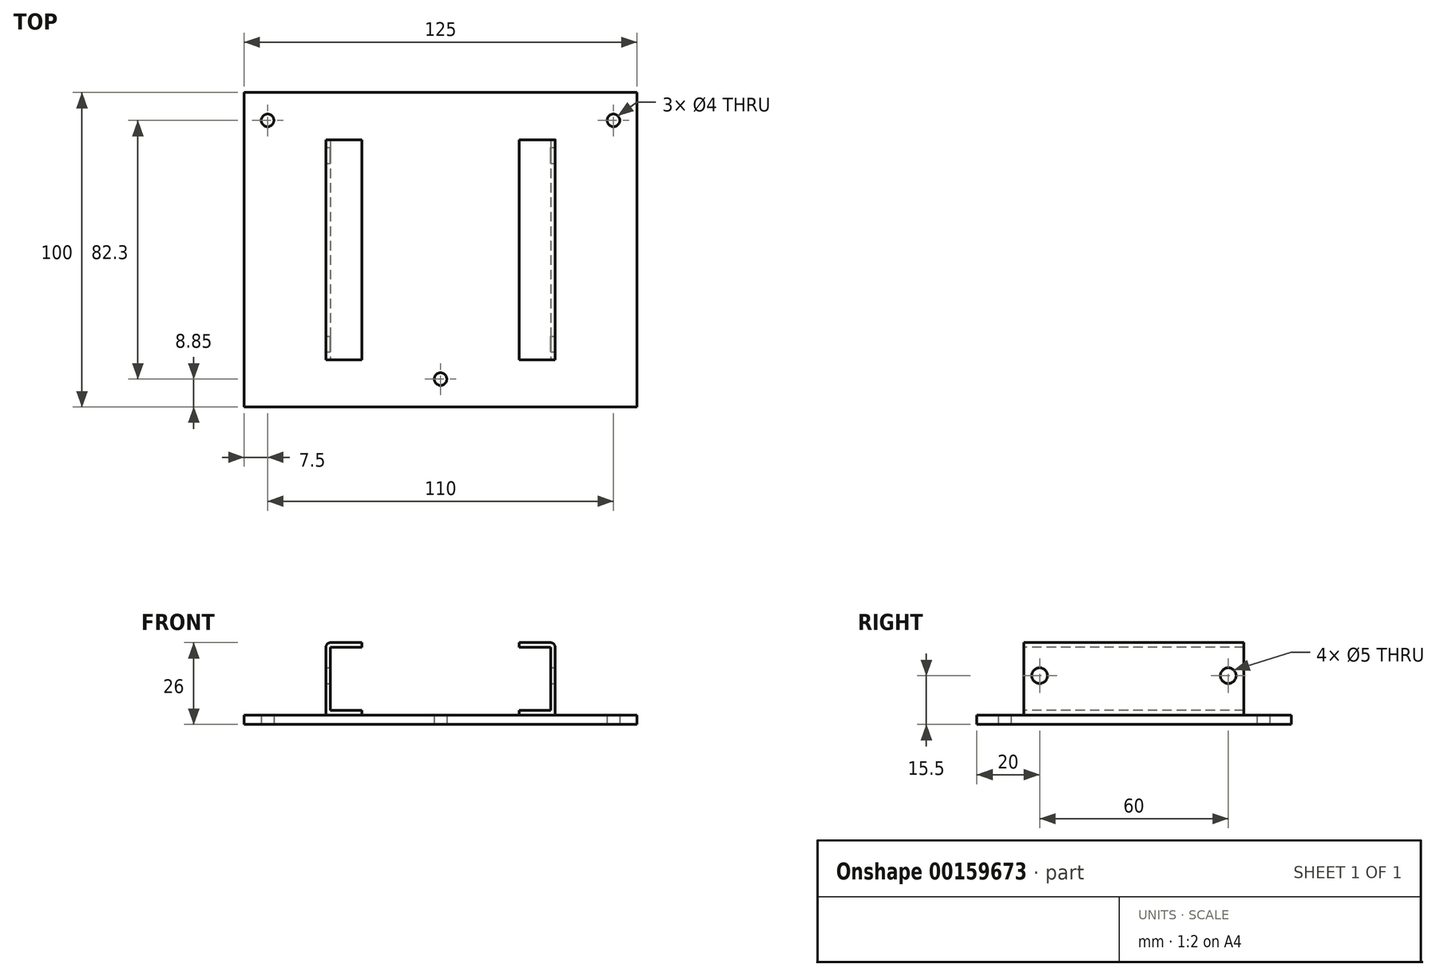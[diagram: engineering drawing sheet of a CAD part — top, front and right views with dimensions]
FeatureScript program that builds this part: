
annotation { "Feature Type Name" : "Feature", "Feature Type Description" : "" }
export const myFeature = defineFeature(function(context is Context, id is Id, definition is map)
    precondition{}
    {
        {
            var Q0;
            Q0=qCreatedBy(makeId("Top.planeOp"),FACE);
            var sketch = newSketch(context, id + "F0", { "sketchPlane" : qUnion([Q0])});
            skCircle(sketch, "E0", {"center": v(55, 41.15) * mm, "radius": 2 * mm});
            skCircle(sketch, "E1.MirrorC", {"center": v(-55, 41.15) * mm, "radius": 2 * mm});
            skCircle(sketch, "E2", {"center": v(0, -41.15) * mm, "radius": 2 * mm});
            skLineSegment(sketch, "E3", {"start": v(35, 35) * mm, "end": v(35, -35) * mm, "construction": true});
            skLineSegment(sketch, "E4", {"start": v(-62.5, 50) * mm, "end": v(-62.5, -50) * mm});
            skLineSegment(sketch, "E5.MirrorCS", {"start": v(62.5, 50) * mm, "end": v(62.5, -50) * mm});
            skLineSegment(sketch, "E6", {"start": v(-62.5, -50) * mm, "end": v(62.5, -50) * mm});
            skLineSegment(sketch, "E7", {"start": v(-62.5, 50) * mm, "end": v(62.5, 50) * mm});
            skLineSegment(sketch, "E8.MirrorCS", {"start": v(-35, 35) * mm, "end": v(-35, -35) * mm, "construction": true});
            skSolve(sketch);
        }
        {
            var Q0;
            Q0=makeQuery(id+"F0.imprint","IMPRINT",FACE,{"disambiguationData":[TD([[makeQuery(id+"F0.imprint","IMPRINT",EDGE,{"derivedFrom":sQuery(id+"F0.wireOp",EDGE,"E0")}),-1.0]])]});
            extrude(context, id + "F1", {"entities" : qUnion([Q0]), "depth" : 3 * mm});
        }
        {
            var Q0;
            Q0=qCreatedBy(makeId("Front.planeOp"),FACE);
            cPlane(context, id + "F2", {"entities" : qUnion([Q0]), "cplaneType" : CPlaneType.OFFSET, "offset" : 35 * mm, "width" : 150 * mm, "height" : 150 * mm});
        }
        {
            var Q0;
            Q0=qCreatedBy(id+"F2.planeOp",FACE);
            var sketch = newSketch(context, id + "F3", { "sketchPlane" : qUnion([Q0])});
            skLineSegment(sketch, "E9", {"start": v(35, 4.5) * mm, "end": v(35, 24.5) * mm});
            skLineSegment(sketch, "E10", {"start": v(35, 24.5) * mm, "end": v(25, 24.5) * mm});
            skLineSegment(sketch, "E11", {"start": v(35, 4.5) * mm, "end": v(25, 4.5) * mm});
            skLineSegment(sketch, "E12.0", {"start": v(36.5, 26) * mm, "end": v(25, 26) * mm});
            skLineSegment(sketch, "E12.1", {"start": v(36.5, 3) * mm, "end": v(36.5, 26) * mm});
            skLineSegment(sketch, "E12.2", {"start": v(36.5, 3) * mm, "end": v(25, 3) * mm});
            skLineSegment(sketch, "E13", {"start": v(25, 24.5) * mm, "end": v(25, 26) * mm});
            skLineSegment(sketch, "E14", {"start": v(25, 3) * mm, "end": v(25, 4.5) * mm});
            skLineSegment(sketch, "E15.MirrorCS", {"start": v(-36.5, 3) * mm, "end": v(-36.5, 26) * mm});
            skLineSegment(sketch, "E16.MirrorCS", {"start": v(-35, 4.5) * mm, "end": v(-35, 24.5) * mm});
            skLineSegment(sketch, "E17.MirrorCS", {"start": v(-35, 4.5) * mm, "end": v(-25, 4.5) * mm});
            skLineSegment(sketch, "E18.MirrorCS", {"start": v(-36.5, 3) * mm, "end": v(-25, 3) * mm});
            skLineSegment(sketch, "E19.MirrorCS", {"start": v(-36.5, 26) * mm, "end": v(-25, 26) * mm});
            skLineSegment(sketch, "E20.MirrorCS", {"start": v(-35, 24.5) * mm, "end": v(-25, 24.5) * mm});
            skLineSegment(sketch, "E21.MirrorCS", {"start": v(-25, 3) * mm, "end": v(-25, 4.5) * mm});
            skLineSegment(sketch, "E22.MirrorCS", {"start": v(-25, 24.5) * mm, "end": v(-25, 26) * mm});
            skSolve(sketch);
        }
        {
            var Q0;
            Q0 = qSketchRegion(id + "F3", true);
            extrude(context, id + "F4", {"entities" : qUnion([Q0]), "operationType" : NewBodyOperationType.ADD, "oppositeDirection" : true, "depth" : 70 * mm});
        }
        {
            var Q0;
            Q0=makeQuery(id+"F4.opExtrude","SWEPT_FACE",FACE,{"disambiguationData":[OSD([sQuery(id+"F3.wireOp",EDGE,"E12.1")])]});
            var sketch = newSketch(context, id + "F5", { "sketchPlane" : qUnion([Q0])});
            skCircle(sketch, "E23", {"center": v(-30, 15.5) * mm, "radius": 2.5 * mm});
            skCircle(sketch, "E24.MirrorC", {"center": v(30, 15.5) * mm, "radius": 2.5 * mm});
            skSolve(sketch);
        }
        {
            var Q0;
            Q0 = qSketchRegion(id + "F5", true);
            extrude(context, id + "F6", {"entities" : qUnion([Q0]), "operationType" : NewBodyOperationType.REMOVE, "endBound" : BoundingType.THROUGH_ALL, "oppositeDirection" : true, "depth" : 25 * mm});
        }
        {
            var Q0;
            Q0=makeQuery(id+"F4.opExtrude","SWEPT_EDGE",EDGE,{"disambiguationData":[OSD([sQuery(id+"F3.wireOp",EDGE,"E12.0"),sQuery(id+"F3.wireOp",EDGE,"E12.1")])]});
            var Q1;
            Q1=makeQuery(id+"F4.opExtrude","SWEPT_EDGE",EDGE,{"disambiguationData":[OSD([sQuery(id+"F3.wireOp",EDGE,"E15.MirrorCS"),sQuery(id+"F3.wireOp",EDGE,"E19.MirrorCS")])]});
            fillet(context, id + "F7", {"entities" : qUnion([Q0, Q1]), "radius" : 1.5 * mm, "tangentPropagation" : true, "allowEdgeOverflow" : false});
        }
    });
